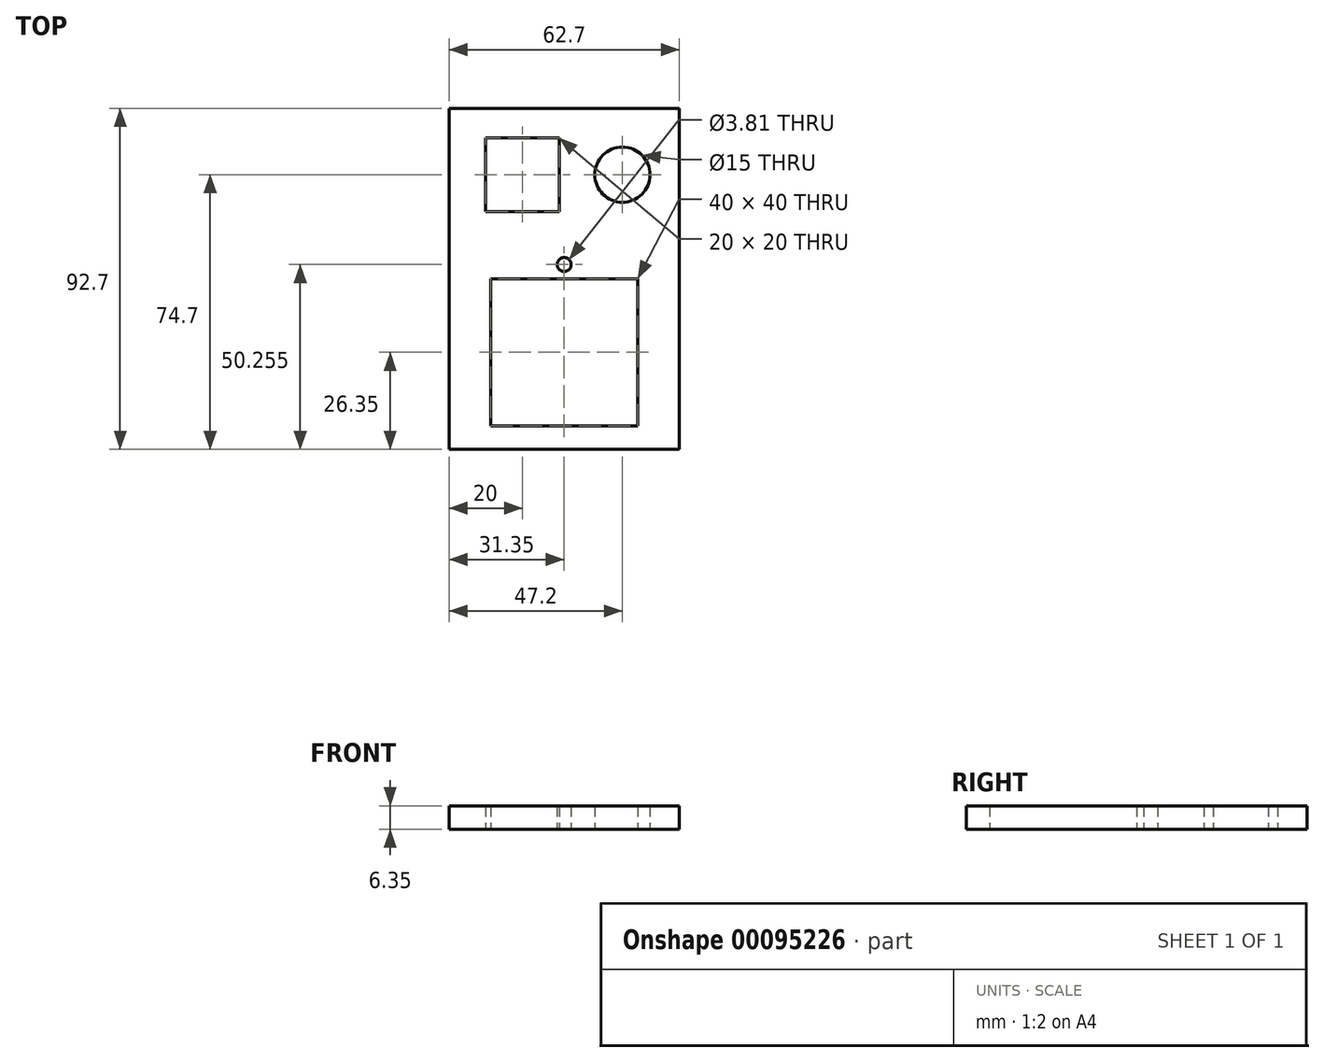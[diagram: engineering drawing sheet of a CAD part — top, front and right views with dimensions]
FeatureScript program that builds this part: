
annotation { "Feature Type Name" : "Feature", "Feature Type Description" : "" }
export const myFeature = defineFeature(function(context is Context, id is Id, definition is map)
    precondition{}
    {
        {
            var Q0;
            Q0=qCreatedBy(makeId("Top.planeOp"),FACE);
            var sketch = newSketch(context, id + "F0", { "sketchPlane" : qUnion([Q0])});
            skLineSegment(sketch, "E0.bottom", {"start": v(31.35, 46.35) * mm, "end": v(-31.35, 46.35) * mm});
            skLineSegment(sketch, "E0.top", {"start": v(31.35, -46.35) * mm, "end": v(-31.35, -46.35) * mm});
            skLineSegment(sketch, "E0.left", {"start": v(31.35, 46.35) * mm, "end": v(31.35, -46.35) * mm});
            skLineSegment(sketch, "E0.right", {"start": v(-31.35, 46.35) * mm, "end": v(-31.35, -46.35) * mm});
            skPoint(sketch, "E0.middle", {"position": v(0, 0) * mm});
            skLineSegment(sketch, "E1.bottom", {"start": v(20, 0) * mm, "end": v(-20, 0) * mm});
            skLineSegment(sketch, "E1.top", {"start": v(20, -40) * mm, "end": v(-20, -40) * mm});
            skLineSegment(sketch, "E1.left", {"start": v(20, 0) * mm, "end": v(20, -40) * mm});
            skLineSegment(sketch, "E1.right", {"start": v(-20, 0) * mm, "end": v(-20, -40) * mm});
            skPoint(sketch, "E1.middle", {"position": v(0, -20) * mm});
            skLineSegment(sketch, "E2", {"start": v(0, -40) * mm, "end": v(0, -46.35) * mm});
            skCircle(sketch, "E3", {"center": v(0, 3.9) * mm, "radius": 1.9 * mm});
            skLineSegment(sketch, "E4", {"start": v(0, 2) * mm, "end": v(0, 0) * mm});
            skLineSegment(sketch, "E5.bottom", {"start": v(-1.35, 18.35) * mm, "end": v(-21.35, 18.35) * mm});
            skLineSegment(sketch, "E5.top", {"start": v(-1.35, 38.35) * mm, "end": v(-21.35, 38.35) * mm});
            skLineSegment(sketch, "E5.left", {"start": v(-1.35, 18.35) * mm, "end": v(-1.35, 38.35) * mm});
            skLineSegment(sketch, "E5.right", {"start": v(-21.35, 18.35) * mm, "end": v(-21.35, 38.35) * mm});
            skPoint(sketch, "E5.middle", {"position": v(-11.35, 28.35) * mm});
            skLineSegment(sketch, "E6", {"start": v(-21.35, 38.35) * mm, "end": v(-21.35, 46.35) * mm, "construction": true});
            skLineSegment(sketch, "E7", {"start": v(-21.35, 38.35) * mm, "end": v(-31.35, 38.35) * mm, "construction": true});
            skCircle(sketch, "E8", {"center": v(15.85, 28.35) * mm, "radius": 7.5 * mm});
            skLineSegment(sketch, "E9", {"start": v(23.35, 28.35) * mm, "end": v(31.35, 28.35) * mm, "construction": true});
            skSolve(sketch);
        }
        {
            var Q0;
            {var subQ3=sQuery(id+"F0.wireOp",EDGE,"E0.bottom");Q0=makeQuery(id+"F0.imprint","IMPRINT",FACE,{"disambiguationData":[TD([[makeQuery(id+"F0.imprint","IMPRINT",EDGE,{"derivedFrom":subQ3}),1.0]])]});}
            extrude(context, id + "F1", {"entities" : qUnion([Q0]), "depth" : 6.35 * mm});
        }
    });
